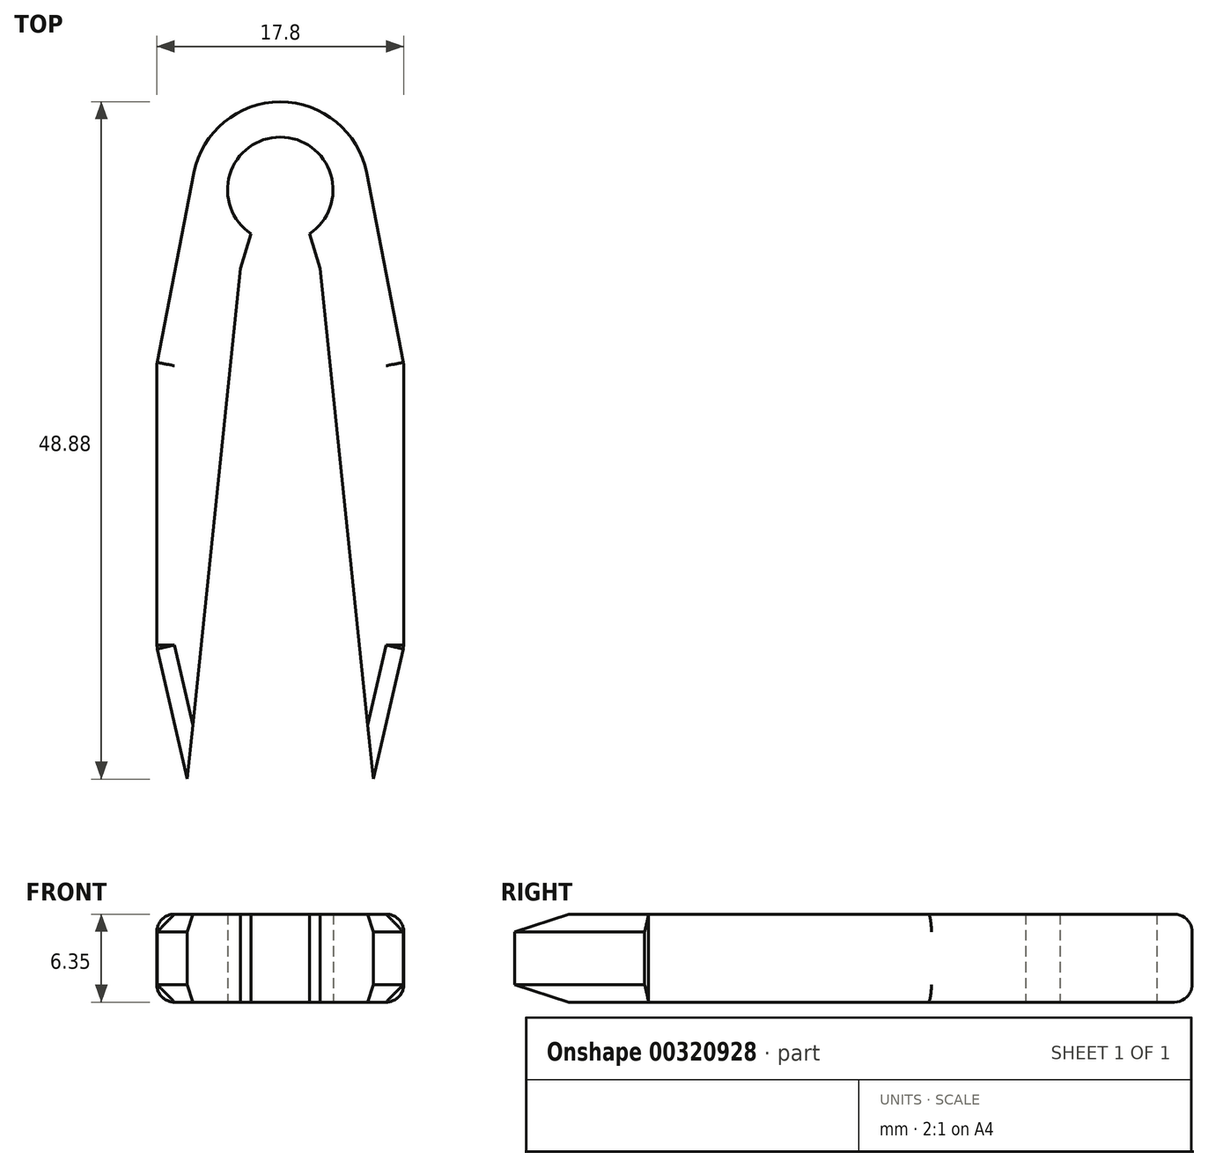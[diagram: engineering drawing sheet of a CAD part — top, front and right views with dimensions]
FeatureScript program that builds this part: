
annotation { "Feature Type Name" : "Feature", "Feature Type Description" : "" }
export const myFeature = defineFeature(function(context is Context, id is Id, definition is map)
    precondition{}
    {
        {
            var Q0;
            Q0=qCreatedBy(makeId("Top.planeOp"),FACE);
            var sketch = newSketch(context, id + "F0", { "sketchPlane" : qUnion([Q0])});
            skCircle(sketch, "E0", {"center": v(0, 59.05) * mm, "radius": 6.35 * mm});
            skLineSegment(sketch, "E1", {"start": v(-2.87, 53.38) * mm, "end": v(-6.71, 16.52) * mm});
            skLineSegment(sketch, "E2.MirrorCS", {"start": v(2.87, 53.38) * mm, "end": v(6.71, 16.52) * mm});
            skLineSegment(sketch, "E3", {"start": v(-8.9, 46.47) * mm, "end": v(-6.23, 60.25) * mm});
            skLineSegment(sketch, "E4.MirrorCS", {"start": v(8.9, 46.47) * mm, "end": v(6.23, 60.25) * mm});
            skCircle(sketch, "E5", {"center": v(0, 59.05) * mm, "radius": 3.81 * mm});
            skLineSegment(sketch, "E6", {"start": v(-2.87, 53.38) * mm, "end": v(0, 62.86) * mm});
            skLineSegment(sketch, "E7", {"start": v(2.87, 53.38) * mm, "end": v(0, 62.86) * mm});
            skLineSegment(sketch, "E8", {"start": v(-8.9, 46.47) * mm, "end": v(-8.9, 26.05) * mm});
            skLineSegment(sketch, "E9", {"start": v(-8.9, 26.05) * mm, "end": v(-6.71, 16.52) * mm});
            skLineSegment(sketch, "E10.MirrorCS", {"start": v(8.9, 46.47) * mm, "end": v(8.9, 26.05) * mm});
            skLineSegment(sketch, "E11.MirrorCS", {"start": v(8.9, 26.05) * mm, "end": v(6.71, 16.52) * mm});
            skSolve(sketch);
        }
        {
            var Q0;
            {var subQ0=sQuery(id+"F0.wireOp",EDGE,"E1");Q0=makeQuery(id+"F0.imprint","IMPRINT",FACE,{"disambiguationData":[TD([[makeQuery(id+"F0.imprint","IMPRINT",EDGE,{"derivedFrom":subQ0}),-1.0]])]});}
            var Q1;
            {var subQ0=sQuery(id+"F0.wireOp",EDGE,"E2.MirrorCS");Q1=makeQuery(id+"F0.imprint","IMPRINT",FACE,{"disambiguationData":[TD([[makeQuery(id+"F0.imprint","IMPRINT",EDGE,{"derivedFrom":subQ0}),1.0]])]});}
            var Q2;
            {var subQ1=sQuery(id+"F0.wireOp",EDGE,"E0");var subQ8=makeQuery(id+"F0.imprint","INTERSECT",VERTEX,{"derivedFrom":[subQ1,sQuery(id+"F0.wireOp",EDGE,"E3")]});Q2=makeQuery(id+"F0.imprint","IMPRINT",FACE,{"disambiguationData":[TD([[makeQuery(id+"F0.imprint","IMPRINT",EDGE,{"disambiguationData":[TD([[subQ8,1.0]])],"derivedFrom":subQ1}),1.0]])]});}
            extrude(context, id + "F1", {"entities" : qUnion([Q0, Q1, Q2]), "depth" : 6.35 * mm});
        }
        {
            var Q0;
            Q0=makeQuery(id+"F1.opExtrude","CAP_EDGE",EDGE,{"disambiguationData":[OSD([sQuery(id+"F0.wireOp",EDGE,"E3")])],"isStart":true});
            var Q1;
            Q1=makeQuery(id+"F1.opExtrude","CAP_EDGE",EDGE,{"disambiguationData":[OSD([sQuery(id+"F0.wireOp",EDGE,"E4.MirrorCS")])],"isStart":true});
            var Q2;
            Q2=makeQuery(id+"F1.opExtrude","CAP_EDGE",EDGE,{"disambiguationData":[OSD([sQuery(id+"F0.wireOp",EDGE,"E0")])],"isStart":true});
            var Q3;
            Q3=makeQuery(id+"F1.opExtrude","CAP_EDGE",EDGE,{"disambiguationData":[OSD([sQuery(id+"F0.wireOp",EDGE,"E4.MirrorCS")])],"isStart":false});
            var Q4;
            Q4=makeQuery(id+"F1.opExtrude","CAP_EDGE",EDGE,{"disambiguationData":[OSD([sQuery(id+"F0.wireOp",EDGE,"E3")])],"isStart":false});
            var Q5;
            Q5=makeQuery(id+"F1.opExtrude","CAP_EDGE",EDGE,{"disambiguationData":[OSD([sQuery(id+"F0.wireOp",EDGE,"E0")])],"isStart":false});
            fillet(context, id + "F2", {"entities" : qUnion([Q0, Q1, Q2, Q3, Q4, Q5]), "radius" : 1.27 * mm, "tangentPropagation" : true, "allowEdgeOverflow" : false});
        }
        {
            var Q0;
            Q0=makeQuery(id+"F1.opExtrude","CAP_EDGE",EDGE,{"disambiguationData":[OSD([sQuery(id+"F0.wireOp",EDGE,"E8")])],"isStart":false});
            var Q1;
            Q1=makeQuery(id+"F1.opExtrude","CAP_EDGE",EDGE,{"disambiguationData":[OSD([sQuery(id+"F0.wireOp",EDGE,"E8")])],"isStart":true});
            var Q2;
            Q2=makeQuery(id+"F1.opExtrude","CAP_EDGE",EDGE,{"disambiguationData":[OSD([sQuery(id+"F0.wireOp",EDGE,"E10.MirrorCS")])],"isStart":false});
            var Q3;
            Q3=makeQuery(id+"F1.opExtrude","CAP_EDGE",EDGE,{"disambiguationData":[OSD([sQuery(id+"F0.wireOp",EDGE,"E10.MirrorCS")])],"isStart":true});
            fillet(context, id + "F3", {"entities" : qUnion([Q0, Q1, Q2, Q3]), "radius" : 1.27 * mm, "tangentPropagation" : true, "allowEdgeOverflow" : false});
        }
        {
            var Q0;
            Q0=makeQuery(id+"F1.opExtrude","CAP_EDGE",EDGE,{"disambiguationData":[OSD([sQuery(id+"F0.wireOp",EDGE,"E9")])],"isStart":false});
            var Q1;
            Q1=makeQuery(id+"F1.opExtrude","CAP_EDGE",EDGE,{"disambiguationData":[OSD([sQuery(id+"F0.wireOp",EDGE,"E9")])],"isStart":true});
            var Q2;
            Q2=makeQuery(id+"F1.opExtrude","CAP_EDGE",EDGE,{"disambiguationData":[OSD([sQuery(id+"F0.wireOp",EDGE,"E11.MirrorCS")])],"isStart":false});
            var Q3;
            Q3=makeQuery(id+"F1.opExtrude","CAP_EDGE",EDGE,{"disambiguationData":[OSD([sQuery(id+"F0.wireOp",EDGE,"E11.MirrorCS")])],"isStart":true});
            chamfer(context, id + "F4", {"entities" : qUnion([Q0, Q1, Q2, Q3]), "width" : 1.27 * mm, "tangentPropagation" : true});
        }
    });
